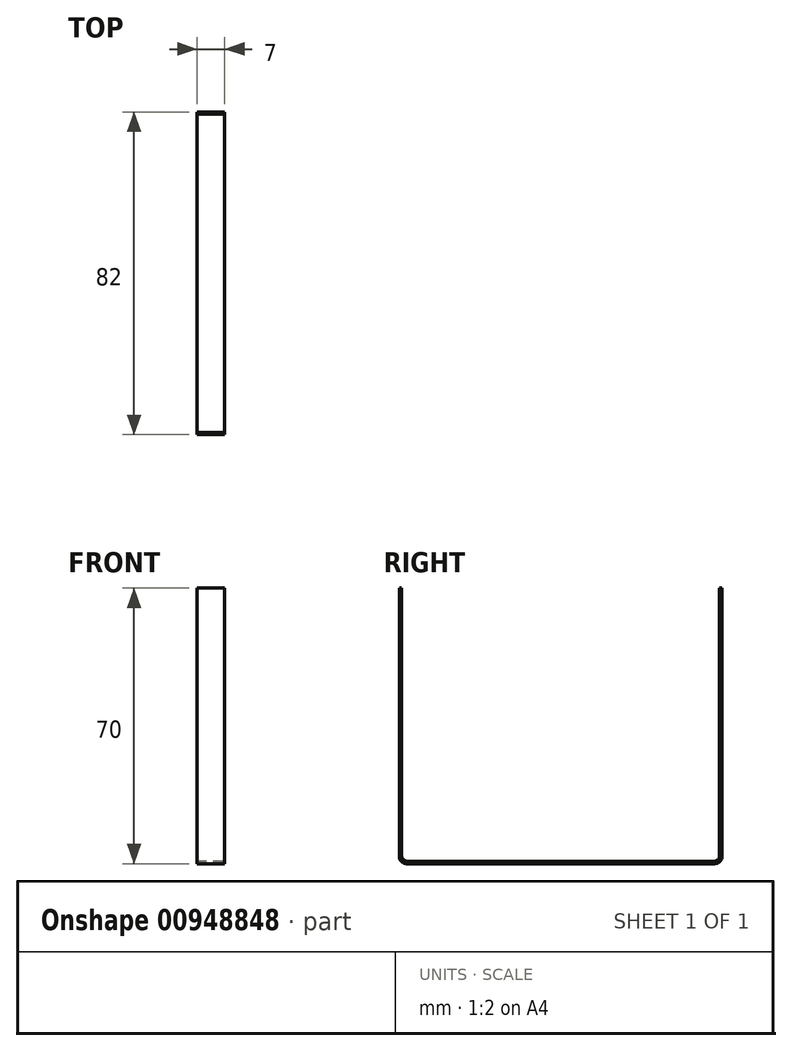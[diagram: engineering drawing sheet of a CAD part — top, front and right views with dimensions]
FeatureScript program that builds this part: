
annotation { "Feature Type Name" : "Feature", "Feature Type Description" : "" }
export const myFeature = defineFeature(function(context is Context, id is Id, definition is map)
    precondition{}
    {
        {
            var Q0;
            Q0=qCreatedBy(makeId("Right.planeOp"),FACE);
            var sketch = newSketch(context, id + "F0", { "sketchPlane" : qUnion([Q0])});
            skLineSegment(sketch, "E0.bottom", {"start": v(-41, 35) * mm, "end": v(-40.4, 35) * mm});
            skLineSegment(sketch, "E0.top", {"start": v(-41, -35) * mm, "end": v(41, -35) * mm});
            skLineSegment(sketch, "E0.left", {"start": v(-41, 35) * mm, "end": v(-41, -35) * mm});
            skLineSegment(sketch, "E0.right", {"start": v(41, 35) * mm, "end": v(41, -35) * mm});
            skPoint(sketch, "E0.middle", {"position": v(0, 0) * mm});
            skLineSegment(sketch, "E1.0", {"start": v(40.4, 35) * mm, "end": v(40.4, -34.4) * mm});
            skLineSegment(sketch, "E1.1", {"start": v(-40.4, -34.4) * mm, "end": v(40.4, -34.4) * mm});
            skLineSegment(sketch, "E1.2", {"start": v(-40.4, 35) * mm, "end": v(-40.4, -34.4) * mm});
            skLineSegment(sketch, "E2.trimOffspring", {"start": v(40.4, 35) * mm, "end": v(41, 35) * mm});
            skSolve(sketch);
        }
        {
            var Q0;
            Q0 = qSketchRegion(id + "F0", true);
            extrude(context, id + "F1", {"entities" : qUnion([Q0]), "depth" : 7 * mm, "offsetDistance" : 25 * mm});
        }
        {
            var Q0;
            Q0=makeQuery(id+"F1.opExtrude","SWEPT_EDGE",EDGE,{"disambiguationData":[OSD([sQuery(id+"F0.wireOp",EDGE,"E1.1"),sQuery(id+"F0.wireOp",EDGE,"E1.2")])]});
            var Q1;
            Q1=makeQuery(id+"F1.opExtrude","SWEPT_EDGE",EDGE,{"disambiguationData":[OSD([sQuery(id+"F0.wireOp",EDGE,"E1.0"),sQuery(id+"F0.wireOp",EDGE,"E1.1")])]});
            fillet(context, id + "F2", {"entities" : qUnion([Q0, Q1]), "radius" : 1.5 * mm, "tangentPropagation" : true, "allowEdgeOverflow" : false});
        }
        {
            var Q0;
            Q0=makeQuery(id+"F1.opExtrude","SWEPT_EDGE",EDGE,{"disambiguationData":[OSD([sQuery(id+"F0.wireOp",EDGE,"E0.top"),sQuery(id+"F0.wireOp",EDGE,"E0.left")])]});
            var Q1;
            Q1=makeQuery(id+"F1.opExtrude","SWEPT_EDGE",EDGE,{"disambiguationData":[OSD([sQuery(id+"F0.wireOp",EDGE,"E0.top"),sQuery(id+"F0.wireOp",EDGE,"E0.right")])]});
            fillet(context, id + "F3", {"entities" : qUnion([Q0, Q1]), "radius" : 1.8 * mm, "tangentPropagation" : true, "allowEdgeOverflow" : false});
        }
    });
